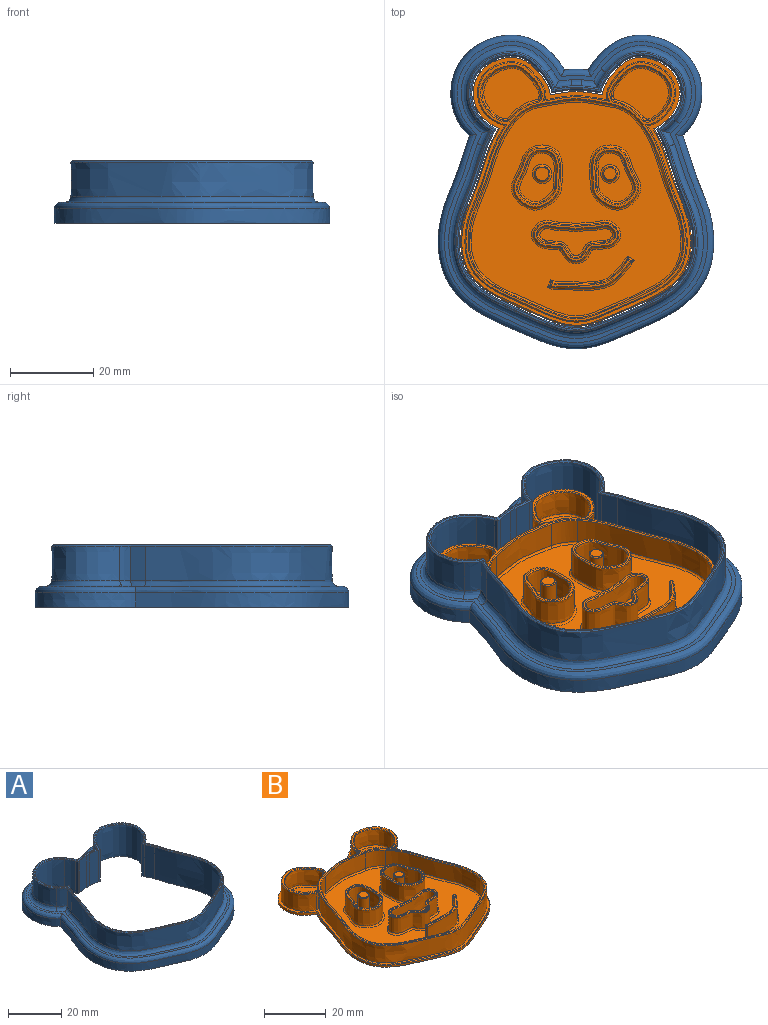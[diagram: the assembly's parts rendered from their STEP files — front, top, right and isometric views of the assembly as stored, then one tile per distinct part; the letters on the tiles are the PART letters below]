
ASSEMBLY  parts=2 mates=1
PART A: 87 faces, bbox 66.5x75.7x15.3 mm
  f0: extruded ~14.7x3.08mm, area 60.1mm2, adj f1,f31,f33,f57
  f1: extruded ~16.8x14.7mm, area 428.2mm2, adj f0,f2,f33,f55
  f2: extruded ~14.7x3.69mm, area 63.2mm2, adj f1,f3,f33,f53
  f3: extruded ~14.7x0.98mm, area 14.8mm2, adj f2,f4,f33,f51
  f4: extruded ~14.7x0.99mm, area 14.7mm2, adj f3,f5,f33,f52
  f5: extruded ~14.7x3.97mm, area 58.8mm2, adj f4,f6,f33,f54
  f6: extruded ~14.7x1.93mm, area 28.4mm2, adj f5,f7,f33,f56
  f7: extruded ~14.7x3.97mm, area 58.8mm2, adj f6,f8,f33,f58
  f8: extruded ~14.7x0.99mm, area 14.7mm2, adj f7,f9,f33,f60
  f9: extruded ~14.7x0.98mm, area 14.7mm2, adj f8,f10,f33,f62
  f10: extruded ~14.7x3.7mm, area 63.2mm2, adj f9,f11,f33,f64
  f11: extruded ~16.92x14.7mm, area 430mm2, adj f10,f12,f33,f66
  f12: extruded ~14.7x3.04mm, area 60.3mm2, adj f11,f13,f33,f68
  f13: extruded ~14.7x0.87mm, area 14.7mm2, adj f12,f14,f33,f70
  f14: extruded ~14.7x0.88mm, area 14.7mm2, adj f13,f15,f33,f69
  f15: extruded ~14.7x3.66mm, area 58.9mm2, adj f14,f16,f33,f67
  f16: extruded ~56.06x43.29mm, area 1799.3mm2, adj f15,f17,f33,f65
  f17: extruded ~14.7x3.65mm, area 58.8mm2, adj f16,f18,f33,f63
  f18: extruded ~14.7x0.88mm, area 14.7mm2, adj f17,f31,f33,f61
  f19: extruded ~18.92x16.35mm, area 272.3mm2, adj f20,f30,f45,f75
  f20: extruded ~8.2x3.14mm, area 33.6mm2, adj f19,f21,f43,f73
  f21: extruded ~8.2x3.66mm, area 33mm2, adj f20,f22,f41,f71
  f22: extruded ~58.07x44.75mm, area 1035mm2, adj f21,f23,f39,f72
  f23: extruded ~8.2x3.67mm, area 33mm2, adj f22,f24,f40,f74
  f24: extruded ~8.2x3.1mm, area 33.7mm2, adj f23,f25,f42,f76
  f25: extruded ~19.03x16.36mm, area 273.3mm2, adj f24,f26,f44,f78
  f26: extruded ~8.2x3.71mm, area 34.8mm2, adj f25,f27,f46,f80
  f27: extruded ~8.2x4mm, area 33.1mm2, adj f26,f28,f48,f82
  f28: extruded ~8.2x2.29mm, area 18.8mm2, adj f27,f29,f50,f81
  f29: extruded ~8.2x4.01mm, area 33.1mm2, adj f28,f30,f49,f79
  f30: extruded ~8.2x3.71mm, area 34.9mm2, adj f19,f29,f47,f77
  f31: extruded ~14.7x0.89mm, area 14.7mm2, adj f0,f18,f33,f59
  f32: plane 67.2x58.05mm, normal (0,0,1), area 110.5mm2, adj f39,f40,f41,f42,f43,f44,f45,f46
  f33: plane 75.37x66.21mm, normal (0,0,-1), area 1180.5mm2, adj f0,f1,f2,f3,f4,f5,f6,f7
  f34: extruded ~27.29x24.18mm, area 174.4mm2, adj f33,f35,f37,f86
  f35: extruded ~66.14x51.17mm, area 499.5mm2, adj f33,f34,f36,f84
  f36: extruded ~27.41x24.2mm, area 175mm2, adj f33,f35,f37,f83
  f37: extruded ~5.62x3.5mm, area 19.7mm2, adj f33,f34,f36,f85
  f38: plane 72.37x63.21mm, normal (0,0,1), area 240.5mm2, adj f71,f72,f73,f74,f75,f76,f77,f78
  f39: bspline ~58.24x44.78mm, area 53.6mm2, adj f22,f32,f40,f41
  f40: bspline ~4.22x2.14mm, area 1.8mm2, adj f23,f32,f39,f42
  f41: bspline ~4.02x2.05mm, area 1.8mm2, adj f21,f32,f39,f43
  f42: bspline ~3.68x3.13mm, area 1.8mm2, adj f24,f32,f40,f44
  f43: bspline ~3.72x3.06mm, area 1.8mm2, adj f20,f32,f41,f45
  f44: bspline ~19.15x16.38mm, area 13.9mm2, adj f25,f32,f42,f46
  f45: bspline ~18.95x16.36mm, area 13.9mm2, adj f19,f32,f43,f47
  f46: bspline ~4.05x2.34mm, area 1.8mm2, adj f26,f32,f44,f48
  f47: bspline ~4.05x2.37mm, area 1.8mm2, adj f30,f32,f45,f49
  f48: bspline ~4.49x0.9mm, area 1.8mm2, adj f27,f32,f46,f50
  f49: bspline ~4.49x0.89mm, area 1.8mm2, adj f29,f32,f47,f50
  f50: bspline ~2.29x0.35mm, area 1mm2, adj f28,f32,f48,f49
  f51: bspline ~1.13x0.53mm, area 0.4mm2, adj f3,f32,f52,f53
  f52: bspline ~1.09x0.47mm, area 0.4mm2, adj f4,f32,f51,f54
  f53: bspline ~3.88x2.45mm, area 1.8mm2, adj f2,f32,f51,f55
  f54: bspline ~4.02x0.8mm, area 1.7mm2, adj f5,f32,f52,f56
  f55: bspline ~17.36x14.93mm, area 12.6mm2, adj f1,f32,f53,f57
  f56: bspline ~1.96x0.34mm, area 0.8mm2, adj f6,f32,f54,f58
  f57: bspline ~3.32x2.92mm, area 1.8mm2, adj f0,f32,f55,f59
  f58: bspline ~4.02x0.81mm, area 1.7mm2, adj f7,f32,f56,f60
  f59: bspline ~1.04x0.74mm, area 0.4mm2, adj f31,f32,f57,f61
  f60: bspline ~1.04x0.46mm, area 0.4mm2, adj f8,f32,f58,f62
  f61: bspline ~1.03x0.75mm, area 0.4mm2, adj f18,f32,f59,f63
  f62: bspline ~1.07x0.52mm, area 0.4mm2, adj f9,f32,f60,f64
  f63: bspline ~3.79x1.92mm, area 1.7mm2, adj f17,f32,f61,f65
  f64: bspline ~3.88x2.43mm, area 1.8mm2, adj f10,f32,f62,f66
  f65: bspline ~56.85x43.7mm, area 52.3mm2, adj f16,f32,f63,f67
  f66: bspline ~17.48x15.03mm, area 12.6mm2, adj f11,f32,f64,f68
  f67: bspline ~3.79x1.91mm, area 1.7mm2, adj f15,f32,f65,f69
  f68: bspline ~3.28x2.98mm, area 1.8mm2, adj f12,f32,f66,f70
  f69: bspline ~1.03x0.74mm, area 0.4mm2, adj f14,f32,f67,f70
  f70: bspline ~1.08x0.78mm, area 0.4mm2, adj f13,f32,f68,f69
  f71: bspline ~5.96x3.78mm, area 8mm2, adj f21,f38,f72,f73
  f72: bspline ~61.21x60.58mm, area 304.2mm2, adj f22,f38,f71,f74
  f73: bspline ~5.53x5.05mm, area 8.5mm2, adj f20,f38,f71,f75
  f74: bspline ~5.98x3.77mm, area 8.1mm2, adj f23,f38,f72,f76
  f75: bspline ~27.3x25.9mm, area 82.4mm2, adj f19,f38,f73,f77
  f76: bspline ~5.21x4.94mm, area 8.6mm2, adj f24,f38,f74,f78
  f77: bspline ~5.78x4.24mm, area 9mm2, adj f30,f38,f75,f79
  f78: bspline ~27.02x25.51mm, area 82.7mm2, adj f25,f38,f76,f80
  f79: bspline ~6.31x2.25mm, area 8.2mm2, adj f29,f38,f77,f81
  f80: bspline ~10.4x7.72mm, area 9mm2, adj f26,f38,f78,f82
  f81: bspline ~2.99x1.56mm, area 5.6mm2, adj f28,f38,f79,f82
  f82: bspline ~6.28x2.26mm, area 8.2mm2, adj f27,f38,f80,f81
  f83: bspline ~28.18x25.65mm, area 115.7mm2, adj f36,f38,f84,f85
  f84: bspline ~66.21x52.91mm, area 338.4mm2, adj f35,f38,f83,f86
  f85: bspline ~12.28x2.2mm, area 15.2mm2, adj f37,f38,f83,f86
  f86: bspline ~28.01x25.47mm, area 115.4mm2, adj f34,f38,f84,f85
PART B: 128 faces, bbox 55.8x64.9x8.3 mm
  f0: plane 51.4x50.41mm, normal (0,0,1), area 1470mm2, adj f58,f60,f61,f62,f63,f64,f65,f67
  f1: plane 64.36x54.99mm, normal (0,0,1), area 174.4mm2, adj f2,f4,f5,f16,f17,f18,f19,f20
  f2: extruded ~18.4x17.03mm, area 38.8mm2, adj f1,f3,f5,f6,f87
  f3: extruded ~55.25x47.61mm, area 99.3mm2, adj f2,f4,f6,f87
  f4: extruded ~18.52x17.13mm, area 38.9mm2, adj f1,f3,f5,f6,f87
  f5: extruded ~12.58x1mm, area 12.7mm2, adj f1,f2,f4,f6
  f6: plane 64.57x55.41mm, normal (0,0,-1), area 2758.2mm2, adj f2,f3,f4,f5
  f7: extruded ~6.25x5.66mm, area 43mm2, adj f8,f30,f70,f126
  f8: extruded ~18.65x6.25mm, area 118mm2, adj f7,f9,f69,f127
  f9: extruded ~6.25x5.54mm, area 41.2mm2, adj f8,f30,f67,f125
  f10: extruded ~6.94x6.25mm, area 51.7mm2, adj f11,f27,f74,f119
  f11: extruded ~6.25x1.13mm, area 7.7mm2, adj f10,f12,f72,f118
  f12: extruded ~14.28x13.08mm, area 189.7mm2, adj f11,f27,f71,f116
  f13: extruded ~6.25x1.29mm, area 8.2mm2, adj f14,f28,f78,f122
  f14: extruded ~14.25x13mm, area 189.6mm2, adj f13,f15,f77,f120
  f15: extruded ~6.25x1.13mm, area 7.8mm2, adj f14,f28,f75,f121
  f16: extruded ~16.39x15.08mm, area 234.6mm2, adj f1,f17,f29,f113
  f17: extruded ~6.75x1.07mm, area 7.4mm2, adj f1,f16,f18,f111
  f18: extruded ~6.75x0.96mm, area 7.7mm2, adj f1,f17,f19,f109
  f19: extruded ~53.23x46.33mm, area 869.5mm2, adj f1,f18,f20,f107
  f20: extruded ~6.75x1.03mm, area 8.2mm2, adj f1,f19,f21,f105
  f21: extruded ~6.75x1.14mm, area 7.8mm2, adj f1,f20,f22,f104
  f22: extruded ~16.53x15.18mm, area 235.2mm2, adj f1,f21,f23,f106
  f23: extruded ~6.75x1.06mm, area 7.5mm2, adj f1,f22,f24,f108
  f24: extruded ~6.75x1.16mm, area 7.9mm2, adj f1,f23,f25,f110
  f25: extruded ~12.91x6.75mm, area 87.9mm2, adj f1,f24,f26,f112
  f26: extruded ~6.75x1.14mm, area 7.8mm2, adj f1,f25,f29,f114
  f27: extruded ~6.25x1.74mm, area 12.2mm2, adj f10,f12,f73,f117
  f28: extruded ~7.31x6.25mm, area 55.4mm2, adj f13,f15,f76,f123
  f29: extruded ~6.75x1.08mm, area 7.6mm2, adj f1,f16,f26,f115
  f30: extruded ~51.36x47.66mm, area 820mm2, adj f7,f9,f68,f124
  f31: plane 62.52x53.32mm, normal (0,0,1), area 91.4mm2, adj f104,f105,f106,f107,f108,f109,f110,f111
  f32: plane 13.28x12.06mm, normal (0,0,1), area 106.7mm2, adj f75,f76,f77,f78
  f33: plane 13.32x12.15mm, normal (0,0,1), area 107mm2, adj f71,f72,f73,f74
  f34: extruded ~18.32x7.42mm, area 267.9mm2, adj f66,f103
  f35: extruded ~20.18x9.41mm, area 314.2mm2, adj f65,f102
  f36: plane 20.51x9.38mm, normal (0,0,1), area 16mm2, adj f102,f103
  f37: plane 17.53x6.45mm, normal (0,0,1), area 56.7mm2, adj f66
  f38: plane 6.25x0.17mm, normal (0.52,0.85,0), area 1.3mm2, adj f64,f79,f85,f100
  f39: extruded ~17.79x6.25mm, area 125.1mm2, adj f63,f79,f81,f96
  f40: plane 6.25x0.18mm, normal (-0.91,0.42,0), area 1.3mm2, adj f61,f81,f83,f95
  f41: extruded ~18.94x6.25mm, area 133.3mm2, adj f62,f83,f85,f99
  f42: plane 18.79x6.42mm, normal (0,0,1), area 10.7mm2, adj f94,f95,f96,f97,f98,f99,f100,f101
  f43: extruded ~14.6x11.26mm, area 259mm2, adj f60,f89
  f44: extruded ~12.61x9.27mm, area 218.8mm2, adj f59,f90
  f45: plane 14.53x11.18mm, normal (0,0,1), area 17.2mm2, adj f89,f90
  f46: plane 11.64x8.3mm, normal (0,0,1), area 54.9mm2, adj f55,f59
  f47: extruded ~14.6x11.28mm, area 258mm2, adj f58,f92
  f48: extruded ~12.61x9.28mm, area 219.5mm2, adj f57,f93
  f49: plane 14.6x11.24mm, normal (0,0,1), area 19.3mm2, adj f92,f93
  f50: plane 11.64x8.29mm, normal (0,0,1), area 56.5mm2, adj f56,f57
  f51: cylinder r=1.73mm len=6.25mm, axis (0,0,-1), area 68.1mm2, adj f56,f88
  f52: plane 2.97x2.97mm, normal (0,0,1), area 6.9mm2, adj f88
  f53: cylinder r=1.85mm len=6.25mm, axis (0,0,-1), area 72.8mm2, adj f55,f91
  f54: plane 3.21x3.21mm, normal (0,0,1), area 8.1mm2, adj f91
  f55: torus R=2.35mm, axis (0,0,1), area 10mm2, adj f46,f53
  f56: torus R=2.23mm, axis (0,0,1), area 9.5mm2, adj f50,f51
  f57: bspline ~12.64x9.29mm, area 26.6mm2, adj f48,f50
  f58: bspline ~15.64x12.3mm, area 33.3mm2, adj f0,f47
  f59: bspline ~12.64x9.3mm, area 26.6mm2, adj f44,f46
  f60: bspline ~15.64x12.3mm, area 33.3mm2, adj f0,f43
  f61: cylinder r=0.5mm len=2.03mm, axis (0.42,0.91,0), area 0.7mm2, adj f0,f40,f82,f84
  f62: bspline ~21.43x7.87mm, area 17.7mm2, adj f0,f41,f84,f86
  f63: bspline ~19.45x7.18mm, area 16.2mm2, adj f0,f39,f80,f82
  f64: cylinder r=0.5mm len=1.97mm, axis (0.85,-0.52,0), area 0.7mm2, adj f0,f38,f80,f86
  f65: bspline ~21.53x10.45mm, area 40.2mm2, adj f0,f35
  f66: bspline ~18.53x7.45mm, area 34.2mm2, adj f34,f37
  f67: bspline ~7.76x4.97mm, area 5.1mm2, adj f0,f9,f68,f69
  f68: bspline ~56.39x51.41mm, area 102.2mm2, adj f0,f30,f67,f70
  f69: bspline ~25.3x2.83mm, area 14.8mm2, adj f0,f8,f67,f70
  f70: bspline ~7.94x5.41mm, area 5.3mm2, adj f0,f7,f68,f69
  f71: bspline ~14.33x13.14mm, area 23.2mm2, adj f12,f33,f72,f73
  f72: bspline ~3.43x1.39mm, area 0.8mm2, adj f11,f33,f71,f74
  f73: bspline ~2.72x1.3mm, area 1.4mm2, adj f27,f33,f71,f74
  f74: bspline ~9.05x6.32mm, area 6.5mm2, adj f10,f33,f72,f73
  f75: bspline ~1.62x1.03mm, area 0.8mm2, adj f15,f32,f76,f77
  f76: bspline ~9.93x5.74mm, area 6.9mm2, adj f28,f32,f75,f78
  f77: bspline ~14.28x13.09mm, area 23.2mm2, adj f14,f32,f75,f78
  f78: bspline ~1.77x0.64mm, area 0.9mm2, adj f13,f32,f76,f77
  f79: cylinder r=0.4mm len=6.25mm, axis (0,0,-1), area 3.8mm2, adj f38,f39,f80,f98
  f80: bspline ~1.01x0.54mm, area 0.2mm2, adj f63,f64,f79
  f81: cylinder r=0.4mm len=6.25mm, axis (0,0,-1), area 3.5mm2, adj f39,f40,f82,f94
  f82: bspline ~1x0.56mm, area 0.2mm2, adj f61,f63,f81
  f83: cylinder r=0.4mm len=6.25mm, axis (0,0,-1), area 4.3mm2, adj f40,f41,f84,f97
  f84: bspline ~1.1x0.64mm, area 0.2mm2, adj f61,f62,f83
  f85: cylinder r=0.4mm len=6.25mm, axis (0,0,-1), area 4mm2, adj f38,f41,f86,f101
  f86: bspline ~1.04x0.57mm, area 0.2mm2, adj f62,f64,f85
  f87: bspline ~55.46x50.79mm, area 46.6mm2, adj f1,f2,f3,f4
  f88: cone r=1.48mm half-angle=45deg, axis (0,0,-1), area 3.6mm2, adj f51,f52
  f89: bspline ~14.78x11.34mm, area 14.3mm2, adj f43,f45
  f90: bspline ~13.27x9.85mm, area 12.7mm2, adj f44,f45
  f91: cone r=1.6mm half-angle=45deg, axis (0,0,-1), area 3.8mm2, adj f53,f54
  f92: bspline ~14.77x11.33mm, area 14.3mm2, adj f47,f49
  f93: bspline ~13.26x9.83mm, area 12.7mm2, adj f48,f49
  f94: cone r=0.15mm half-angle=45deg, axis (0,0,-1), area 0.1mm2, adj f42,f81,f95,f96
  f95: plane 0.31x0.29mm, normal (-0.64,0.3,0.71), area 0.1mm2, adj f40,f42,f94,f97
  f96: bspline ~18.07x5.99mm, area 7.1mm2, adj f39,f42,f94,f98
  f97: cone r=0.15mm half-angle=45deg, axis (0,0,-1), area 0.2mm2, adj f42,f83,f95,f99
  f98: cone r=0.15mm half-angle=45deg, axis (0,0,-1), area 0.1mm2, adj f42,f79,f96,f100
  f99: bspline ~18.94x6.33mm, area 7.5mm2, adj f41,f42,f97,f101
  f100: plane 0.32x0.3mm, normal (0.37,0.6,0.71), area 0.1mm2, adj f38,f42,f98,f101
  f101: cone r=0.15mm half-angle=45deg, axis (0,0,-1), area 0.2mm2, adj f42,f85,f99,f100
  f102: bspline ~20.61x9.54mm, area 17.6mm2, adj f35,f36
  f103: bspline ~18.95x7.93mm, area 15.9mm2, adj f34,f36
  f104: bspline ~1.74x0.38mm, area 0.5mm2, adj f21,f31,f105,f106
  f105: bspline ~1.59x1.16mm, area 0.5mm2, adj f20,f31,f104,f107
  f106: bspline ~16.57x15.23mm, area 12.1mm2, adj f22,f31,f104,f108
  f107: bspline ~53.46x46.35mm, area 45.3mm2, adj f19,f31,f105,f109
  f108: bspline ~1.55x0.81mm, area 0.5mm2, adj f23,f31,f106,f110
  f109: bspline ~1.53x1.12mm, area 0.5mm2, adj f18,f31,f107,f111
  f110: bspline ~1.78x0.55mm, area 0.5mm2, adj f24,f31,f108,f112
  f111: bspline ~1.54x0.44mm, area 0.5mm2, adj f17,f31,f109,f113
  f112: bspline ~12.91x1.06mm, area 4.6mm2, adj f25,f31,f110,f114
  f113: bspline ~16.49x15.13mm, area 12.1mm2, adj f16,f31,f111,f115
  f114: bspline ~1.62x0.52mm, area 0.5mm2, adj f26,f31,f112,f115
  f115: bspline ~1.6x0.76mm, area 0.5mm2, adj f29,f31,f113,f114
  f116: bspline ~14.99x13.63mm, area 10.9mm2, adj f12,f31,f117,f118
  f117: bspline ~1.97x0.93mm, area 0.7mm2, adj f27,f31,f116,f119
  f118: bspline ~1.34x0.78mm, area 0.5mm2, adj f11,f31,f116,f119
  f119: bspline ~7.12x4.39mm, area 2.9mm2, adj f10,f31,f117,f118
  f120: bspline ~14.87x13.53mm, area 10.9mm2, adj f14,f31,f121,f122
  f121: bspline ~1.41x0.85mm, area 0.5mm2, adj f15,f31,f120,f123
  f122: bspline ~1.49x0.39mm, area 0.5mm2, adj f13,f31,f120,f123
  f123: bspline ~7.52x4.9mm, area 3.1mm2, adj f28,f31,f121,f122
  f124: bspline ~52.01x48.09mm, area 46.8mm2, adj f30,f31,f125,f126
  f125: bspline ~5.73x3.61mm, area 2.4mm2, adj f9,f31,f124,f127
  f126: bspline ~5.85x3.94mm, area 2.5mm2, adj f7,f31,f124,f127
  f127: bspline ~18.78x1.69mm, area 6.7mm2, adj f8,f31,f125,f126
PLACE A t=(-21.66,-10.81,-0.9)mm
PLACE B t=(-21.64,-10.78,-0.9)mm
MATE fastened B.f6 <-> A.f33  axis (0,0,-1) through (-21.63,-6,-0.9)mm
